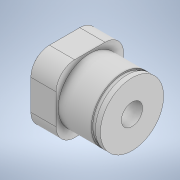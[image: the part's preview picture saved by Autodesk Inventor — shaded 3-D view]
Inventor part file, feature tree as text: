
AUTODESK INVENTOR PART (.ipt)
format: ipt  version: 2020 (Build 240168000, 168)  size: 180,224 bytes
history: native  units: mm
features: extrude x7, sketch x7, fillet x2
ambient origin geometry x8: Origin, YZ Plane, XZ Plane, XY Plane, X Axis, Y Axis, Z Axis, Center Point
bodies: Solid1 (feature_tree)
feature tree (16):
  extrude  "Extrusion1"  Depth=20.32mm
  extrude  "Extrusion2"  Depth=12.7mm
  fillet  "Fillet1"  Radius=12.7mm
  extrude  "Extrusion3"  Depth=5.588mm
  extrude  "Extrusion4"  Depth=1.5mm TaperAngle=0.0deg
  extrude  "Extrusion5"  Depth=25.0mm TaperAngle=0.0deg
  extrude  "Extrusion6"  Depth=5.0mm TaperAngle=0.0deg
  fillet  "Fillet2"  Radius=2.0mm
  extrude  "Extrusion7"  Depth=25.32mm TaperAngle=0.0deg
  sketch  "Sketch1"  dims[d0=20.32mm d1=20.32mm]
  sketch  "Sketch2"  dims[d2=7.62mm d3=0.0mm d4=19.05mm d5=12.7mm d6=0.0mm]
  sketch  "Sketch3"  dims[d7=5.588mm d8=18.25mm]
  sketch  "Sketch4"  dims[d9=2.72mm d10=0.0mm d11=1.5mm d12=0.0mm]
  sketch  "Sketch5"  dims[d13=8.0mm d14=25.0mm d15=0.0mm]
  sketch  "Sketch6"  dims[d16=10.0mm d17=5.0mm d18=0.0mm d19=2.0mm]
  sketch  "Sketch7"  dims[d20=6.4mm d21=25.32mm d22=0.0mm]
